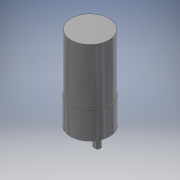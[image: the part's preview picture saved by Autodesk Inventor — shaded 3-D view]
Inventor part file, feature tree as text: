
AUTODESK INVENTOR PART (.ipt)
format: ipt  version: 2017 (Build 210142000, 142)  size: 154,112 bytes
history: native  units: mm
features: other x6, sketch x6, extrude x5, hole x1
ambient origin geometry x8: Origin, YZ Plane, XZ Plane, XY Plane, X Axis, Y Axis, Z Axis, Center Point
bodies: Body1 (feature_tree)
feature tree (18):
  other  "ソリッド1"
  extrude  "押し出し1"  Depth=37.0mm
  extrude  "押し出し2"  Depth=25.0mm TaperAngle=0.0deg
  extrude  "押し出し3"  Depth=36.0mm
  extrude  "押し出し4"  Depth=54.5mm TaperAngle=0.0deg
  hole  "Hole1"  [1 undecoded]
  other  "作業点1"
  other  "作業点2"
  other  "作業平面1"
  extrude  "押し出し5"  Depth=7.0mm
  sketch  "スケッチ1"
  sketch  "スケッチ2"
  sketch  "スケッチ3"
  sketch  "スケッチ4"
  sketch  "スケッチ5"
  other  "作業点3"
  other  "作業点4"
  sketch  "スケッチ7"
note: 1 required parameter value undecoded (feature->parameter linkage not recoverable at this tier; creation-order binding heuristic only, values carry confidence <= 0.55)
